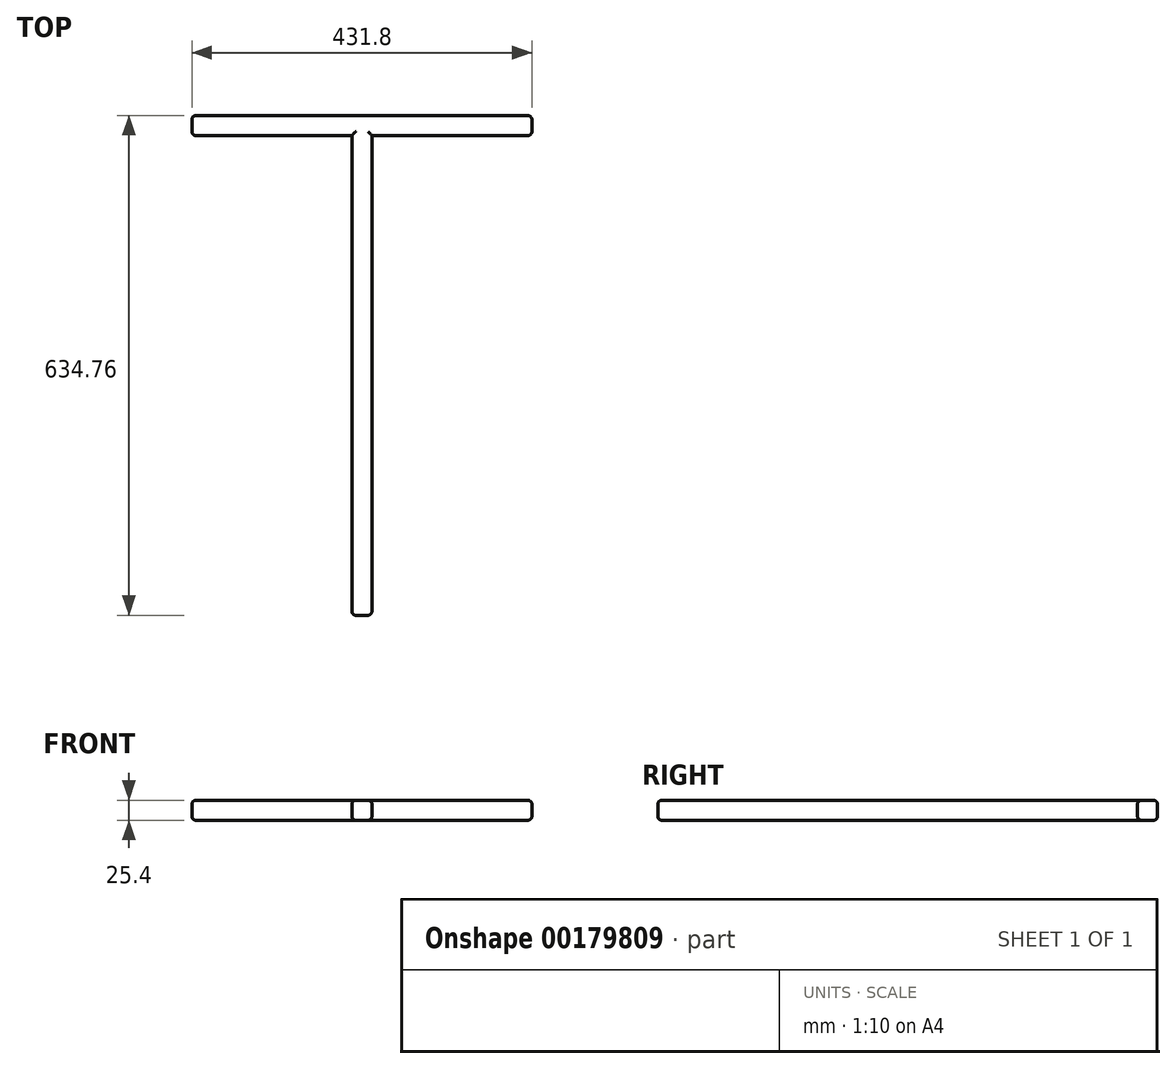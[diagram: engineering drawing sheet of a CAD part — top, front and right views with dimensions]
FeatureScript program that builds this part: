
annotation { "Feature Type Name" : "Feature", "Feature Type Description" : "" }
export const myFeature = defineFeature(function(context is Context, id is Id, definition is map)
    precondition{}
    {
        {
            var Q0;
            Q0=qCreatedBy(makeId("Top.planeOp"),FACE);
            var sketch = newSketch(context, id + "F0", { "sketchPlane" : qUnion([Q0])});
            skLineSegment(sketch, "E0.top", {"start": v(-12.75, -116.82) * mm, "end": v(12.65, -116.82) * mm});
            skLineSegment(sketch, "E0.left", {"start": v(-12.75, 492.78) * mm, "end": v(-12.75, -116.82) * mm});
            skLineSegment(sketch, "E0.right", {"start": v(12.65, 492.78) * mm, "end": v(12.65, -116.82) * mm});
            skLineSegment(sketch, "E1.bottom", {"start": v(-215.95, 517.94) * mm, "end": v(215.85, 517.94) * mm});
            skLineSegment(sketch, "E1.left", {"start": v(-215.95, 517.94) * mm, "end": v(-215.95, 492.54) * mm});
            skLineSegment(sketch, "E1.right", {"start": v(215.85, 517.94) * mm, "end": v(215.85, 492.54) * mm});
            skLineSegment(sketch, "E2", {"start": v(-215.95, 492.54) * mm, "end": v(-12.75, 492.78) * mm});
            skLineSegment(sketch, "E3", {"start": v(12.65, 492.78) * mm, "end": v(215.85, 492.54) * mm});
            skSolve(sketch);
        }
        {
            var Q0;
            Q0=makeQuery(id+"F0.imprint","IMPRINT",FACE,{"disambiguationData":[TD([[makeQuery(id+"F0.imprint","IMPRINT",EDGE,{"derivedFrom":sQuery(id+"F0.wireOp",EDGE,"E0.top")}),1.0]])]});
            extrude(context, id + "F1", {"entities" : qUnion([Q0]), "depth" : 25.4 * mm});
        }
        {
            var Q0;
            Q0=makeQuery(id+"F1.opExtrude","CAP_EDGE",EDGE,{"disambiguationData":[OSD([sQuery(id+"F0.wireOp",EDGE,"E0.right")])],"isStart":false});
            fillet(context, id + "F2", {"entities" : qUnion([Q0]), "radius" : 5.08 * mm, "tangentPropagation" : true, "allowEdgeOverflow" : false});
        }
        {
            var Q0;
            Q0=makeQuery(id+"F1.opExtrude","CAP_EDGE",EDGE,{"disambiguationData":[OSD([sQuery(id+"F0.wireOp",EDGE,"E0.left")])],"isStart":false});
            fillet(context, id + "F3", {"entities" : qUnion([Q0]), "radius" : 5.08 * mm, "tangentPropagation" : true, "allowEdgeOverflow" : false});
        }
        {
            var Q0;
            Q0=makeQuery(id+"F1.opExtrude","CAP_EDGE",EDGE,{"disambiguationData":[OSD([sQuery(id+"F0.wireOp",EDGE,"E0.right")])],"isStart":true});
            fillet(context, id + "F4", {"entities" : qUnion([Q0]), "radius" : 5.08 * mm, "tangentPropagation" : true, "allowEdgeOverflow" : false});
        }
        {
            var Q0;
            Q0=makeQuery(id+"F1.opExtrude","CAP_EDGE",EDGE,{"disambiguationData":[OSD([sQuery(id+"F0.wireOp",EDGE,"E0.left")])],"isStart":true});
            fillet(context, id + "F5", {"entities" : qUnion([Q0]), "radius" : 5.08 * mm, "tangentPropagation" : true, "allowEdgeOverflow" : false});
        }
        {
            var Q0;
            Q0=makeQuery(id+"F1.opExtrude","CAP_EDGE",EDGE,{"disambiguationData":[OSD([sQuery(id+"F0.wireOp",EDGE,"E3")])],"isStart":false});
            fillet(context, id + "F6", {"entities" : qUnion([Q0]), "radius" : 5.08 * mm, "tangentPropagation" : true, "allowEdgeOverflow" : false});
        }
        {
            var Q0;
            Q0=makeQuery(id+"F1.opExtrude","CAP_EDGE",EDGE,{"disambiguationData":[OSD([sQuery(id+"F0.wireOp",EDGE,"E2")])],"isStart":false});
            fillet(context, id + "F7", {"entities" : qUnion([Q0]), "radius" : 5.08 * mm, "tangentPropagation" : true, "allowEdgeOverflow" : false});
        }
        {
            var Q0;
            Q0=makeQuery(id+"F1.opExtrude","CAP_EDGE",EDGE,{"disambiguationData":[OSD([sQuery(id+"F0.wireOp",EDGE,"E3")])],"isStart":true});
            fillet(context, id + "F8", {"entities" : qUnion([Q0]), "radius" : 5.08 * mm, "tangentPropagation" : true, "allowEdgeOverflow" : false});
        }
        {
            var Q0;
            Q0=makeQuery(id+"F1.opExtrude","CAP_EDGE",EDGE,{"disambiguationData":[OSD([sQuery(id+"F0.wireOp",EDGE,"E2")])],"isStart":true});
            fillet(context, id + "F9", {"entities" : qUnion([Q0]), "radius" : 5.08 * mm, "tangentPropagation" : true, "allowEdgeOverflow" : false});
        }
        {
            var Q0;
            Q0=makeQuery(id+"F1.opExtrude","CAP_EDGE",EDGE,{"disambiguationData":[OSD([sQuery(id+"F0.wireOp",EDGE,"E1.bottom")])],"isStart":false});
            fillet(context, id + "F10", {"entities" : qUnion([Q0]), "radius" : 5.08 * mm, "tangentPropagation" : true, "allowEdgeOverflow" : false});
        }
        {
            var Q0;
            Q0=makeQuery(id+"F1.opExtrude","CAP_EDGE",EDGE,{"disambiguationData":[OSD([sQuery(id+"F0.wireOp",EDGE,"E1.bottom")])],"isStart":true});
            fillet(context, id + "F11", {"entities" : qUnion([Q0]), "radius" : 5.08 * mm, "tangentPropagation" : true, "allowEdgeOverflow" : false});
        }
        {
            var Q0;
            Q0=makeQuery(id+"F1.opExtrude","SWEPT_FACE",FACE,{"disambiguationData":[OSD([sQuery(id+"F0.wireOp",EDGE,"E1.right")])]});
            fillet(context, id + "F12", {"entities" : qUnion([Q0]), "radius" : 5.08 * mm, "tangentPropagation" : true, "allowEdgeOverflow" : false});
        }
        {
            var Q0;
            Q0=makeQuery(id+"F1.opExtrude","SWEPT_FACE",FACE,{"disambiguationData":[OSD([sQuery(id+"F0.wireOp",EDGE,"E1.left")])]});
            fillet(context, id + "F13", {"entities" : qUnion([Q0]), "radius" : 5.08 * mm, "tangentPropagation" : true, "allowEdgeOverflow" : false});
        }
        {
            var Q0;
            Q0=makeQuery(id+"F1.opExtrude","SWEPT_FACE",FACE,{"disambiguationData":[OSD([sQuery(id+"F0.wireOp",EDGE,"E0.top")])]});
            fillet(context, id + "F14", {"entities" : qUnion([Q0]), "radius" : 5.08 * mm, "tangentPropagation" : true, "allowEdgeOverflow" : false});
        }
    });
